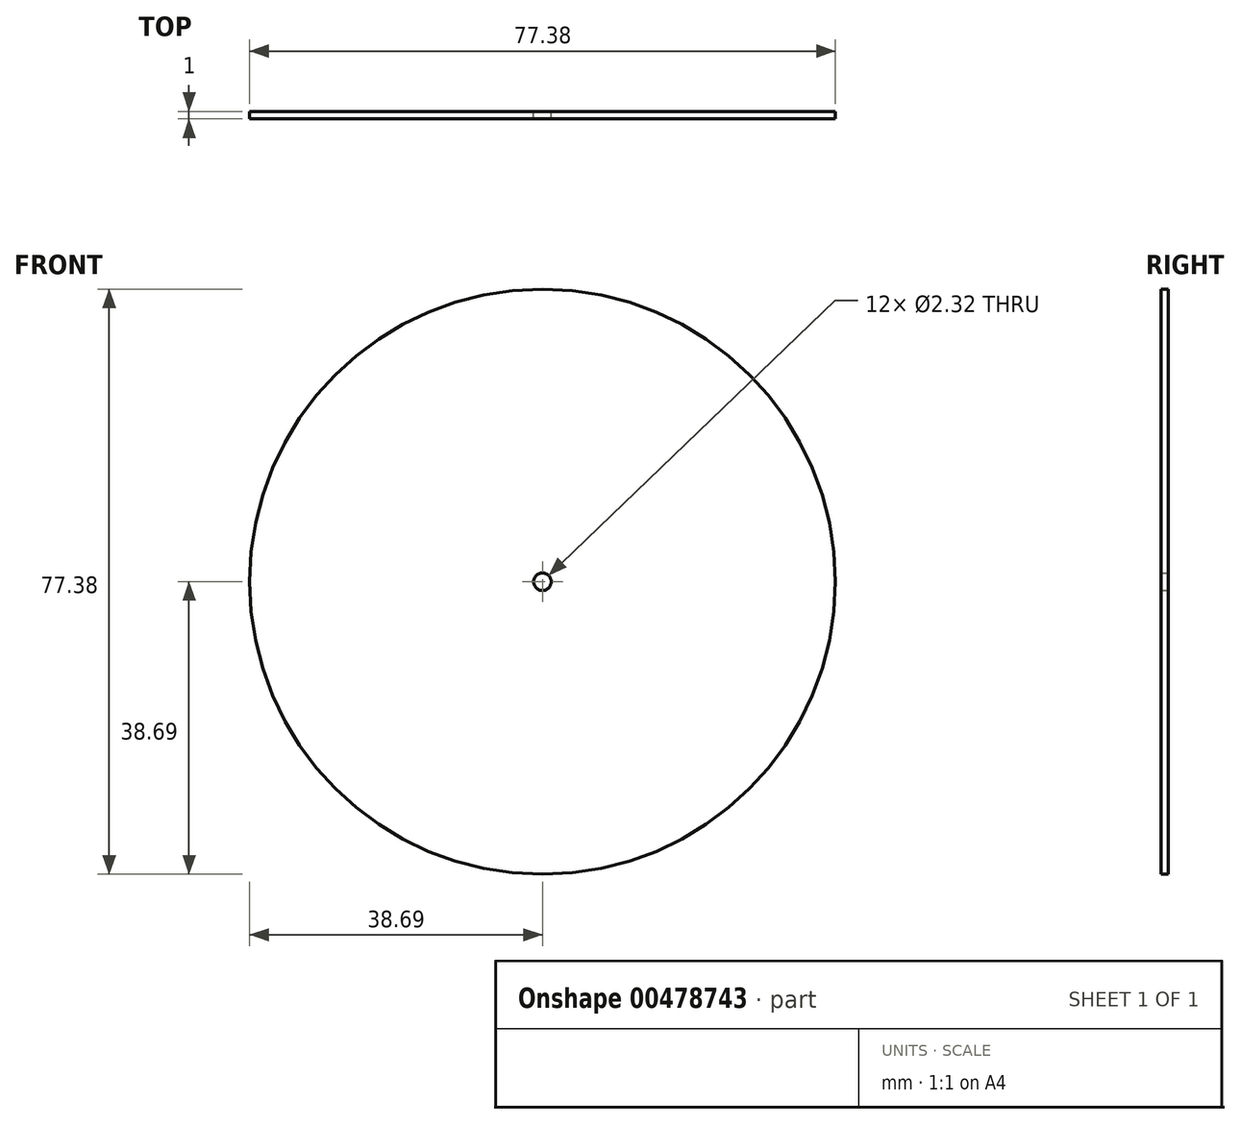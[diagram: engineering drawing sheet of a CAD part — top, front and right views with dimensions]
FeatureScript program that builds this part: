
annotation { "Feature Type Name" : "Feature", "Feature Type Description" : "" }
export const myFeature = defineFeature(function(context is Context, id is Id, definition is map)
    precondition{}
    {
        {
            var Q0;
            Q0=qCreatedBy(makeId("Front.planeOp"),FACE);
            var sketch = newSketch(context, id + "F0", { "sketchPlane" : qUnion([Q0])});
            skCircle(sketch, "E0", {"center": v(0, 0) * mm, "radius": 38.7 * mm});
            skCircle(sketch, "E1", {"center": v(0, 0) * mm, "radius": 1.16 * mm});
            skSolve(sketch);
        }
        {
            var Q0;
            Q0=makeQuery(id+"F0.imprint","IMPRINT",FACE,{"disambiguationData":[TD([[makeQuery(id+"F0.imprint","IMPRINT",EDGE,{"derivedFrom":sQuery(id+"F0.wireOp",EDGE,"E0")}),1.0]])]});
            extrude(context, id + "F1", {"entities" : qUnion([Q0]), "depth" : 1 * mm});
        }
    });
